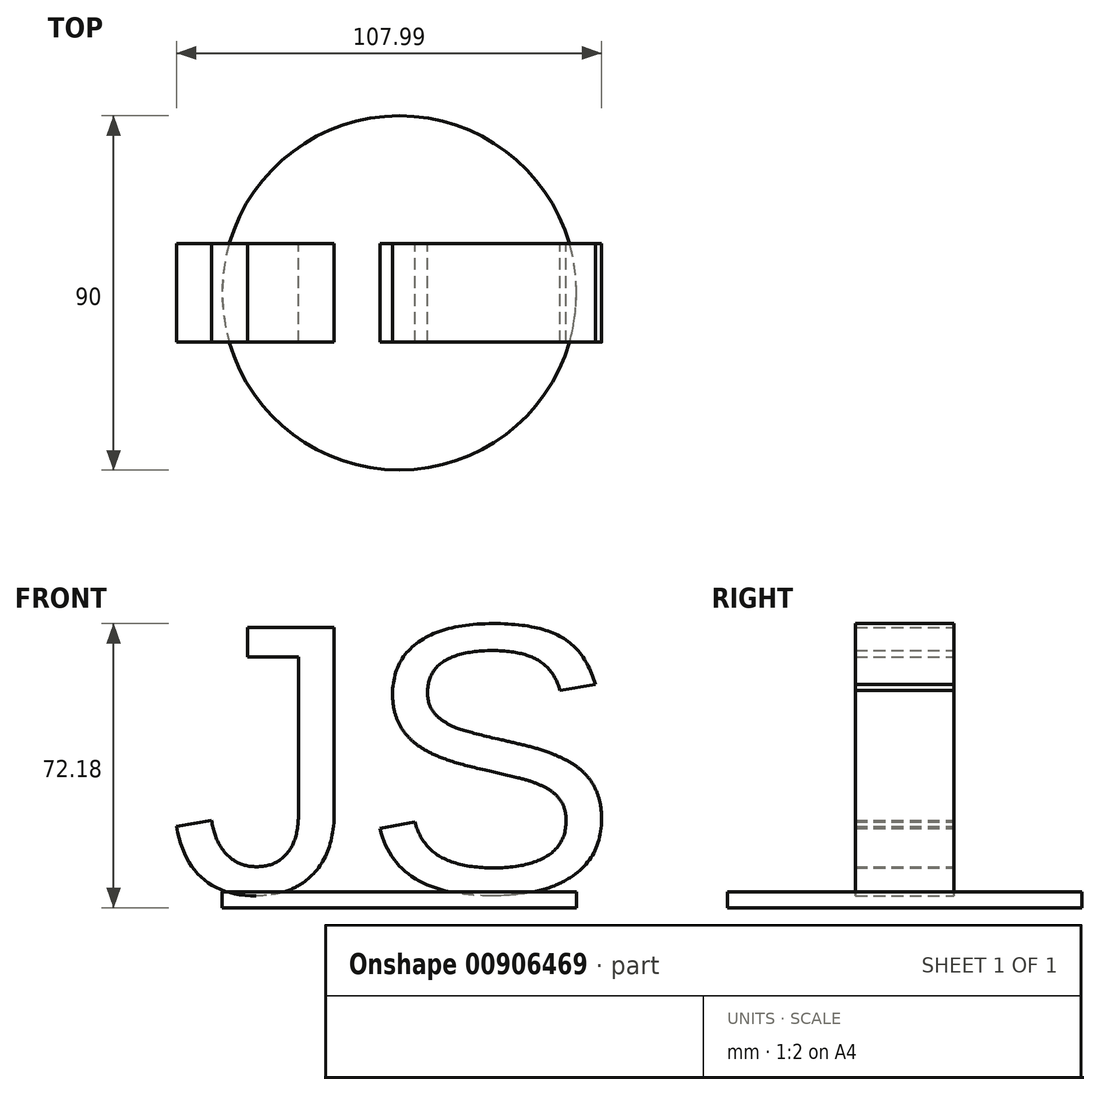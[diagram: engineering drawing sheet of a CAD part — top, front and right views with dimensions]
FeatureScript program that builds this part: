
annotation { "Feature Type Name" : "Feature", "Feature Type Description" : "" }
export const myFeature = defineFeature(function(context is Context, id is Id, definition is map)
    precondition{}
    {
        {
            var Q0;
            Q0=qCreatedBy(makeId("Front.planeOp"),FACE);
            var sketch = newSketch(context, id + "F0", { "sketchPlane" : qUnion([Q0])});
            skText(sketch, "E0", { "text": "JS", "fontName": "Arimo-Regular.ttf"});
            const initialGuessF0  = {"E0": [-0.05815, 0, 1, 0, 0.07034]};
            skSetInitialGuess(sketch, initialGuessF0);
            skSolve(sketch);
        }
        {
            var Q0;
            Q0 = qSketchRegion(id + "F0", true);
            extrude(context, id + "F1", {"entities" : qUnion([Q0]), "endBound" : BoundingType.SYMMETRIC, "depth" : 25 * mm, "offsetDistance" : 25 * mm});
        }
        {
            var Q0;
            Q0=makeQuery(id+"F1.opExtrude","SWEPT_EDGE",EDGE,{"disambiguationData":[OSD([sQuery(id+"F0.wireOp",EDGE,"E0.sketch_text.stroke-14"),sQuery(id+"F0.wireOp",EDGE,"E0.sketch_text.stroke-15")])]});
            cPoint(context, id + "F2", {"entities" : qUnion([Q0]), "parameter" : 0.5});
        }
        {
            var Q0;
            Q0=makeQuery(id+"F1.opExtrude","CAP_VERTEX",VERTEX,{"disambiguationData":[OSD([sQuery(id+"F0.wireOp",EDGE,"E0.sketch_text.stroke-0"),sQuery(id+"F0.wireOp",EDGE,"E0.sketch_text.stroke-12")])],"isStart":true});
            var Q1;
            Q1=makeQuery(id+"F1.opExtrude","CAP_VERTEX",VERTEX,{"disambiguationData":[OSD([sQuery(id+"F0.wireOp",EDGE,"E0.sketch_text.stroke-14"),sQuery(id+"F0.wireOp",EDGE,"E0.sketch_text.stroke-15")])],"isStart":true});
            var Q2;
            Q2 = qCreatedBy(id + "F2" ,VERTEX);
            cPlane(context, id + "F3", {"entities" : qUnion([Q0, Q1, Q2]), "cplaneType" : CPlaneType.THREE_POINT, "offset" : 25 * mm, "width" : 150 * mm, "height" : 150 * mm});
        }
        {
            var Q0;
            Q0=qCreatedBy(id+"F3.planeOp",FACE);
            var sketch = newSketch(context, id + "F4", { "sketchPlane" : qUnion([Q0])});
            skCircle(sketch, "E1", {"center": v(0, 0) * mm, "radius": 45 * mm});
            skSolve(sketch);
        }
        {
            var Q0;
            Q0 = qSketchRegion(id + "F4", true);
            extrude(context, id + "F5", {"entities" : qUnion([Q0]), "depth" : 1 * mm, "offsetDistance" : 25 * mm, "hasSecondDirection" : true, "secondDirectionOppositeDirection" : true, "secondDirectionDepth" : 3 * mm});
        }
    });
